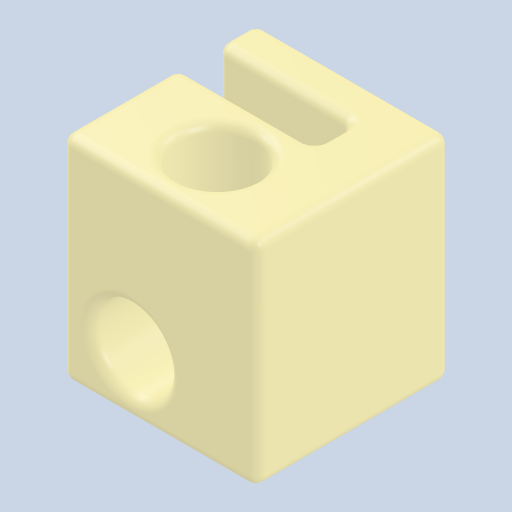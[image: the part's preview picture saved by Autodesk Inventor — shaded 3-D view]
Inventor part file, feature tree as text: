
AUTODESK INVENTOR PART (.ipt)
format: ipt  version: 2023 (Build 270158000, 158)  size: 260,608 bytes
history: native  units: in
note: dims shown in document units (in); Inventor stores cm internally (conversion verified against a paired STEP export)
features: other x5, extrude x4, hole x2, projected_geometry x2, fillet x1, mirror x1, sketch x1
ambient origin geometry x8: Origin, YZ Plane, XZ Plane, XY Plane, X Axis, Y Axis, Z Axis, Center Point
bodies: Solid1 (feature_tree)
feature tree (16):
  extrude  "Ex:Initial"  Depth=0.3937in
  hole  "Hole:PostAttach"  [1 undecoded]
  extrude  "Ex:ProbeSlot1"  Depth=0.0197in
  hole  "Hole:FixProbe"  [1 undecoded]
  extrude  "Ex:ProbeSlot2"  Depth=0.0787in
  fillet  "Fillet1"  Radius=0.1181in
  mirror  "Mirror1"
  extrude  "Extrusion4"  Depth=0.0787in
  other  "Sk:Base"
  other  "Sk:PostAttach"
  other  "Sk:ProbeSlot1"
  other  "Sk:FixProbe"
  projected_geometry  "Projected Loop1"
  other  "Sk:ProbeSlot2"
  projected_geometry  "Projected Loop2"
  sketch  "Sketch6"  dims[d0=0.3937in d1=0.3937in d2=0.1969in d3=0.1969in d4=0.3937in d5=0.0in d6=0.1575in d7=0.1181in d8=0.119in d9=0.0787in d10=0.5635in d11=0.189in d12=0.8108in d13=0.0787in d14=0.1181in d15=0.0787in d16=0.0394in d17=0.0in d18=0.2756in d19=0.1378in d20=0.1181in d21=0.1575in d22=0.2362in d23=0.1575in d24=0.0787in d25=90.0deg d26=0.2362in d27=0.8108in d28=0.0197in d29=0.0197in d30=0.1969in d31=0.1181in d32=0.0in d33=0.0in d34=0.3937in d35=0.0in d36=0.0197in d37=0.0344in]
note: 2 required parameter values undecoded (feature->parameter linkage not recoverable at this tier; creation-order binding heuristic only, values carry confidence <= 0.55)
